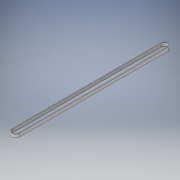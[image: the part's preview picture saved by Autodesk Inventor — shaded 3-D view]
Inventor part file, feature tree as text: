
AUTODESK INVENTOR PART (.ipt)
format: ipt  version: 2019 (Build 230136000, 136)  size: 105,472 bytes
history: native  units: mm
features: extrude x1, sketch x1
ambient origin geometry x8: Origin, YZ Plane, XZ Plane, XY Plane, X Axis, Y Axis, Z Axis, Center Point
bodies: Solid1 (feature_tree)
feature tree (2):
  extrude  "Extrusion1"  Depth=15.0mm
  sketch  "Sketch1"  dims[d0=15.0mm d1=700.0mm d2=3.0mm d3=15.0mm d4=0.0mm]
